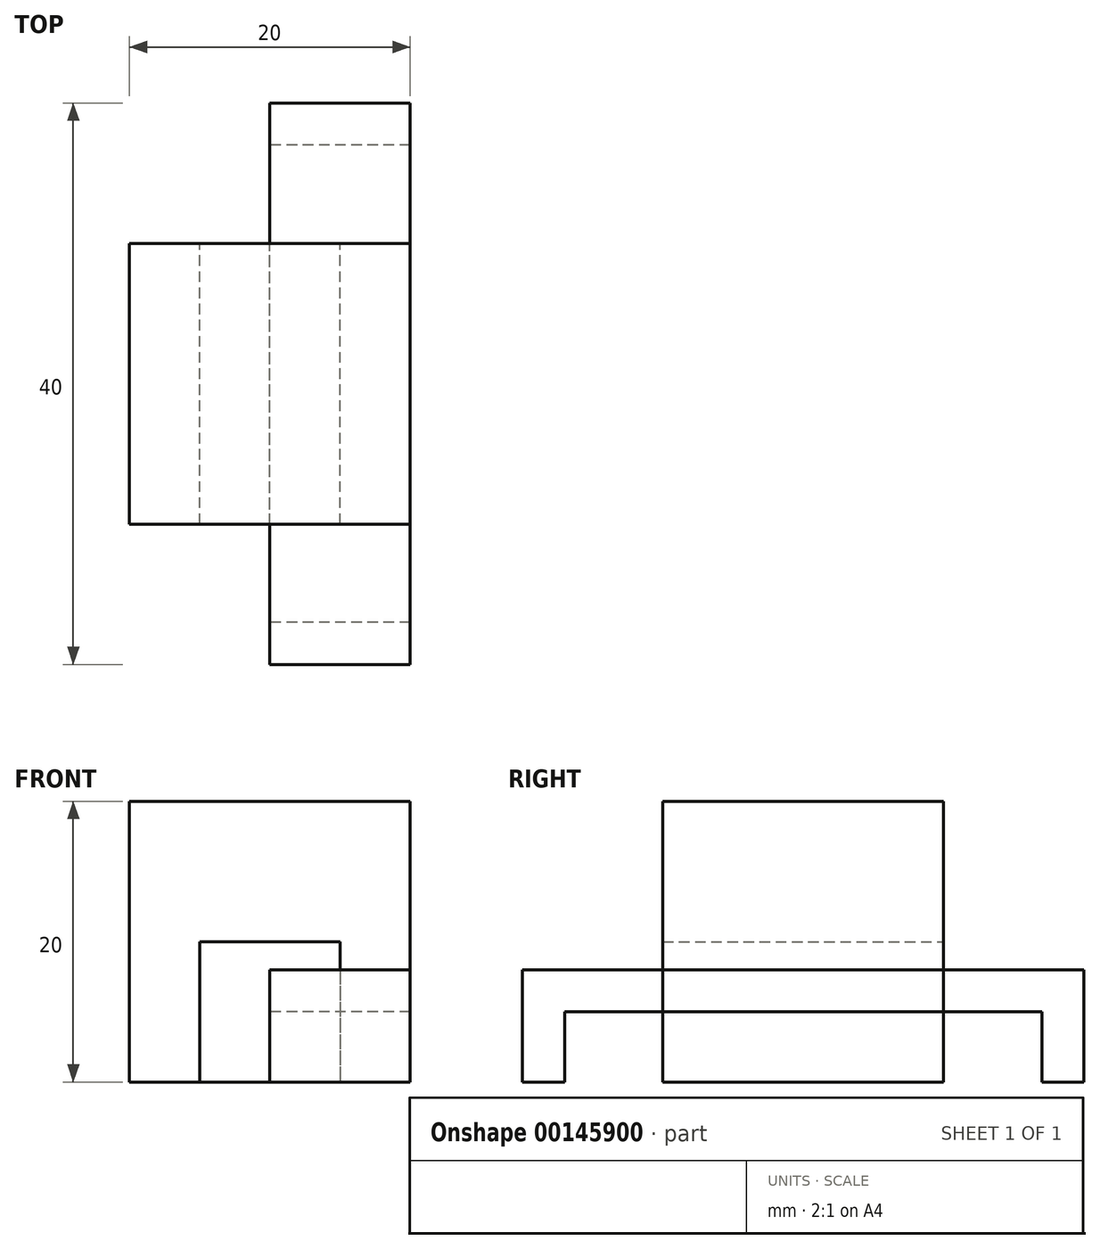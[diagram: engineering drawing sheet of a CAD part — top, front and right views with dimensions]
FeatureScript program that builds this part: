
annotation { "Feature Type Name" : "Feature", "Feature Type Description" : "" }
export const myFeature = defineFeature(function(context is Context, id is Id, definition is map)
    precondition{}
    {
        {
            var Q0;
            Q0=qCreatedBy(makeId("Top.planeOp"),FACE);
            var sketch = newSketch(context, id + "F0", { "sketchPlane" : qUnion([Q0])});
            skLineSegment(sketch, "E0.bottom", {"start": v(10, -10) * mm, "end": v(-10, -10) * mm});
            skLineSegment(sketch, "E0.top", {"start": v(10, 10) * mm, "end": v(-10, 10) * mm});
            skLineSegment(sketch, "E0.left", {"start": v(10, -10) * mm, "end": v(10, 10) * mm});
            skLineSegment(sketch, "E0.right", {"start": v(-10, -10) * mm, "end": v(-10, 10) * mm});
            skPoint(sketch, "E0.middle", {"position": v(0, 0) * mm});
            skSolve(sketch);
        }
        {
            var Q0;
            Q0 = qSketchRegion(id + "F0", true);
            extrude(context, id + "F1", {"entities" : qUnion([Q0]), "depth" : 20 * mm});
        }
        {
            var Q0;
            Q0=qCreatedBy(makeId("Top.planeOp"),FACE);
            var sketch = newSketch(context, id + "F2", { "sketchPlane" : qUnion([Q0])});
            skLineSegment(sketch, "E1.bottom", {"start": v(5, -10) * mm, "end": v(-5, -10) * mm});
            skLineSegment(sketch, "E1.top", {"start": v(5, 10) * mm, "end": v(-5, 10) * mm});
            skLineSegment(sketch, "E1.left", {"start": v(5, -10) * mm, "end": v(5, 10) * mm});
            skLineSegment(sketch, "E1.right", {"start": v(-5, -10) * mm, "end": v(-5, 10) * mm});
            skPoint(sketch, "E1.middle", {"position": v(0, 0) * mm});
            skSolve(sketch);
        }
        {
            var Q0;
            Q0 = qSketchRegion(id + "F2", true);
            extrude(context, id + "F3", {"entities" : qUnion([Q0]), "depth" : 10 * mm});
        }
        {
            var Q0;
            Q0=qCreatedBy(makeId("Right.planeOp"),FACE);
            var sketch = newSketch(context, id + "F4", { "sketchPlane" : qUnion([Q0])});
            skLineSegment(sketch, "E2.bottom", {"start": v(-20, 0) * mm, "end": v(-17, 0) * mm});
            skLineSegment(sketch, "E2.top", {"start": v(-20, 8) * mm, "end": v(-17, 8) * mm});
            skLineSegment(sketch, "E2.left", {"start": v(-20, 0) * mm, "end": v(-20, 8) * mm});
            skLineSegment(sketch, "E2.right", {"start": v(-17, 0) * mm, "end": v(-17, 8) * mm});
            skLineSegment(sketch, "E3.bottom", {"start": v(-17, 8) * mm, "end": v(0, 8) * mm});
            skLineSegment(sketch, "E3.top", {"start": v(-17, 5) * mm, "end": v(0, 5) * mm});
            skLineSegment(sketch, "E3.left", {"start": v(-17, 8) * mm, "end": v(-17, 5) * mm});
            skLineSegment(sketch, "E3.right", {"start": v(0, 8) * mm, "end": v(0, 5) * mm});
            skLineSegment(sketch, "E4.MirrorCS", {"start": v(20, 0) * mm, "end": v(17, 0) * mm});
            skLineSegment(sketch, "E5.MirrorCS", {"start": v(20, 8) * mm, "end": v(17, 8) * mm});
            skLineSegment(sketch, "E6.MirrorCS", {"start": v(20, 0) * mm, "end": v(20, 8) * mm});
            skLineSegment(sketch, "E7.MirrorCS", {"start": v(17, 0) * mm, "end": v(17, 8) * mm});
            skLineSegment(sketch, "E8.MirrorCS", {"start": v(17, 8) * mm, "end": v(0, 8) * mm});
            skLineSegment(sketch, "E9.MirrorCS", {"start": v(17, 5) * mm, "end": v(0, 5) * mm});
            skLineSegment(sketch, "E10.MirrorCS", {"start": v(17, 8) * mm, "end": v(17, 5) * mm});
            skSolve(sketch);
        }
        {
            var Q0;
            Q0 = qSketchRegion(id + "F4", true);
            extrude(context, id + "F5", {"entities" : qUnion([Q0]), "depth" : 10 * mm});
        }
    });
